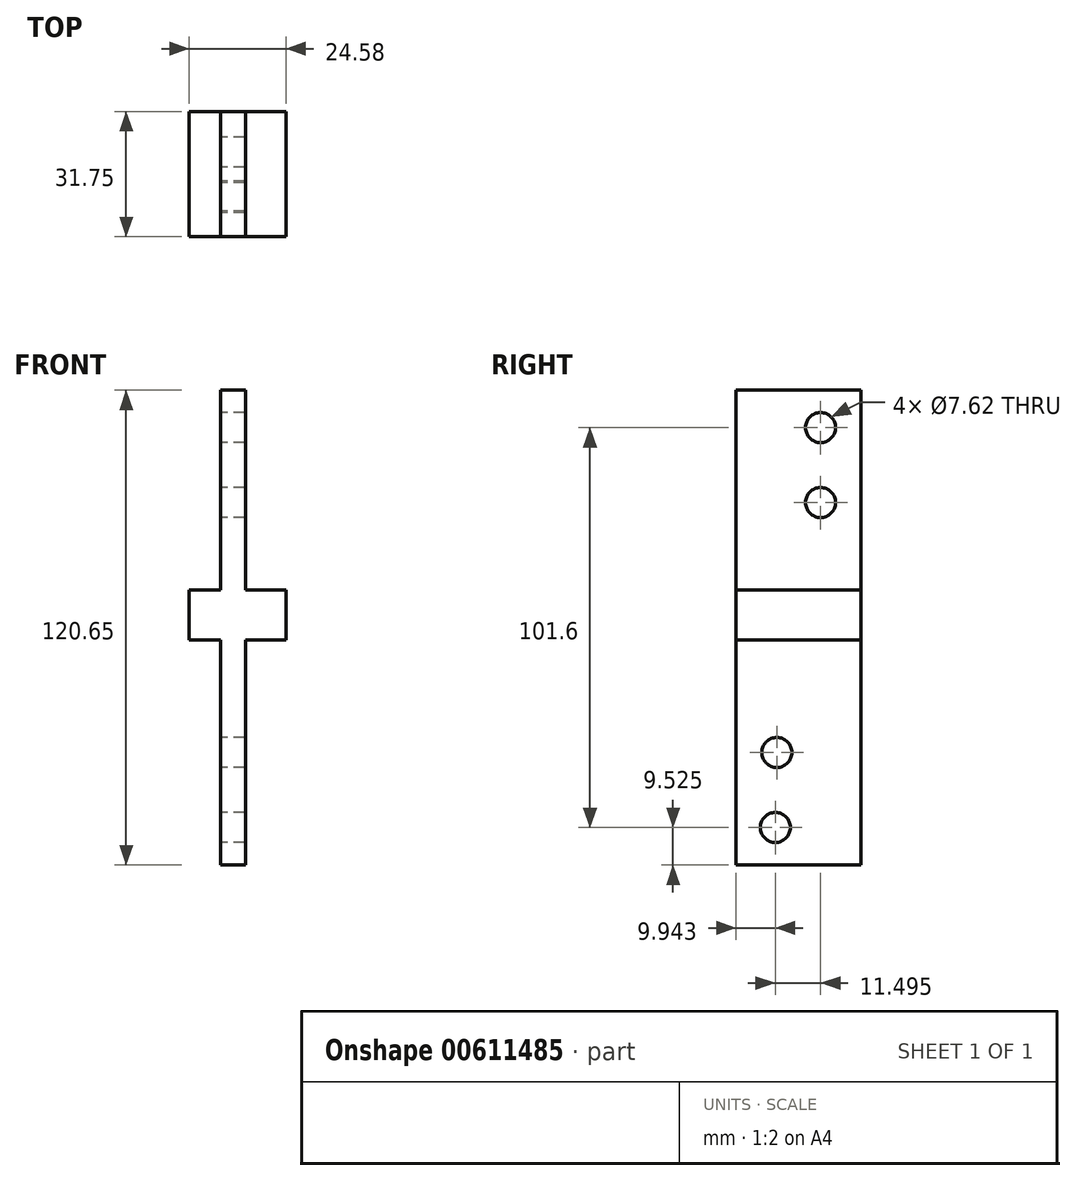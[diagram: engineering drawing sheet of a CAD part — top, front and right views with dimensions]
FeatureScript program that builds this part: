
annotation { "Feature Type Name" : "Feature", "Feature Type Description" : "" }
export const myFeature = defineFeature(function(context is Context, id is Id, definition is map)
    precondition{}
    {
        {
            var Q0;
            Q0=qCreatedBy(makeId("Front.planeOp"),FACE);
            var sketch = newSketch(context, id + "F0", { "sketchPlane" : qUnion([Q0])});
            skLineSegment(sketch, "E0", {"start": v(0, 0) * mm, "end": v(0, 50.8) * mm});
            skLineSegment(sketch, "E1", {"start": v(0, 50.8) * mm, "end": v(6.35, 50.8) * mm});
            skLineSegment(sketch, "E2", {"start": v(6.35, 50.8) * mm, "end": v(6.35, 0) * mm});
            skLineSegment(sketch, "E3", {"start": v(6.35, 0) * mm, "end": v(16.66, 0) * mm});
            skLineSegment(sketch, "E4", {"start": v(16.66, 0) * mm, "end": v(16.66, -12.7) * mm});
            skLineSegment(sketch, "E5", {"start": v(16.66, -12.7) * mm, "end": v(6.35, -12.7) * mm});
            skLineSegment(sketch, "E6", {"start": v(6.35, -12.7) * mm, "end": v(6.35, -69.85) * mm});
            skLineSegment(sketch, "E7", {"start": v(6.35, -69.85) * mm, "end": v(0, -69.85) * mm});
            skLineSegment(sketch, "E8", {"start": v(0, -69.85) * mm, "end": v(0, -12.7) * mm});
            skLineSegment(sketch, "E9", {"start": v(0, -12.7) * mm, "end": v(-7.92, -12.7) * mm});
            skLineSegment(sketch, "E10", {"start": v(-7.92, -12.7) * mm, "end": v(-7.92, 0) * mm});
            skLineSegment(sketch, "E11", {"start": v(-7.92, 0) * mm, "end": v(0, 0) * mm});
            skSolve(sketch);
        }
        {
            var Q0;
            Q0 = qSketchRegion(id + "F0", true);
            extrude(context, id + "F1", {"entities" : qUnion([Q0]), "depth" : 31.75 * mm, "offsetDistance" : 25.4 * mm});
        }
        {
            var Q0;
            Q0=makeQuery(id+"F1.opExtrude","SWEPT_FACE",FACE,{"disambiguationData":[OSD([sQuery(id+"F0.wireOp",EDGE,"E0")])]});
            var sketch = newSketch(context, id + "F2", { "sketchPlane" : qUnion([Q0])});
            skCircle(sketch, "E12", {"center": v(10.31, 41.27) * mm, "radius": 3.81 * mm});
            skSolve(sketch);
        }
        {
            var Q0;
            Q0=makeQuery(id+"F1.opExtrude","SWEPT_FACE",FACE,{"disambiguationData":[OSD([sQuery(id+"F0.wireOp",EDGE,"E0")])]});
            var sketch = newSketch(context, id + "F3", { "sketchPlane" : qUnion([Q0])});
            skCircle(sketch, "E13", {"center": v(10.31, 22.23) * mm, "radius": 3.81 * mm});
            skSolve(sketch);
        }
        {
            var Q0;
            Q0=makeQuery(id+"F1.opExtrude","SWEPT_FACE",FACE,{"disambiguationData":[OSD([sQuery(id+"F0.wireOp",EDGE,"E8")])]});
            var sketch = newSketch(context, id + "F4", { "sketchPlane" : qUnion([Q0])});
            skCircle(sketch, "E14", {"center": v(21.44, -41.28) * mm, "radius": 3.8 * mm});
            skCircle(sketch, "E15", {"center": v(21.8, -60.33) * mm, "radius": 3.81 * mm});
            skSolve(sketch);
        }
        {
            var Q0;
            Q0=sQuery(id+"F2.wireOp",VERTEX,"E12.center");
            var Q1;
            Q1=sQuery(id+"F3.wireOp",VERTEX,"E13.center");
            var Q2;
            Q2=sQuery(id+"F4.wireOp",VERTEX,"E14.center");
            var Q3;
            Q3=sQuery(id+"F4.wireOp",VERTEX,"E15.center");
            var Q4;
            Q4=makeQuery(id+"F1.opExtrude","SWEPT_BODY",BODY,{"disambiguationData":[OSD([sQuery(id+"F0.wireOp",EDGE,"E0"),sQuery(id+"F0.wireOp",EDGE,"E1"),sQuery(id+"F0.wireOp",EDGE,"E2"),sQuery(id+"F0.wireOp",EDGE,"E3"),sQuery(id+"F0.wireOp",EDGE,"E4"),sQuery(id+"F0.wireOp",EDGE,"E5"),sQuery(id+"F0.wireOp",EDGE,"E6"),sQuery(id+"F0.wireOp",EDGE,"E7"),sQuery(id+"F0.wireOp",EDGE,"E8"),sQuery(id+"F0.wireOp",EDGE,"E9"),sQuery(id+"F0.wireOp",EDGE,"E10"),sQuery(id+"F0.wireOp",EDGE,"E11")])]});
            hole(context, id + "F5", {"style" : HoleStyle.SIMPLE, "endStyle" : HoleEndStyle.THROUGH, "holeDiameter" : 7.62 * mm, "majorDiameter" : 6.35 * mm, "isTappedThrough" : true, "tappedDepth" : 12.7 * mm, "tapClearance" : 3, "locations" : qUnion([Q0, Q1, Q2, Q3]), "scope" : qUnion([Q4])});
        }
    });
